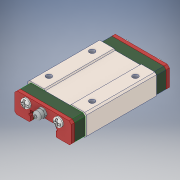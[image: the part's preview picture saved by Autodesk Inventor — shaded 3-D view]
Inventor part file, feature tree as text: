
AUTODESK INVENTOR PART (.ipt)
format: ipt  version: 2018 (Build 220112000, 112)  size: 868,352 bytes
history: native  units: in
note: dims shown in document units (in); Inventor stores cm internally (conversion verified against a paired STEP export)
features: chamfer x3, mirror x3, fillet x2, other x2
ambient origin geometry x8: Origin, YZ Plane, XZ Plane, XY Plane, X Axis, Y Axis, Z Axis, Center Point
bodies: Solid1 (feature_tree), Solid2 (feature_tree), Solid3 (feature_tree), Solid4 (feature_tree), Solid5 (feature_tree), Solid6 (feature_tree), Solid7 (feature_tree), Solid8 (feature_tree), Solid9 (feature_tree), Solid10 (feature_tree)
feature tree (10):
  chamfer  "Chamfer8"  [1 undecoded]
  chamfer  "Chamfer9"  [1 undecoded]
  chamfer  "Chamfer10"  [1 undecoded]
  fillet  "Fillet3"  [1 undecoded]
  mirror  "Mirror9"
  mirror  "Mirror10[1]"
  mirror  "Mirror10[2]"
  fillet  "Fillet5"  [1 undecoded]
  other  "Cut-Extrude9[1]"
  other  "Cut-Extrude9[2]"
note: 5 required parameter values undecoded (feature->parameter linkage not recoverable at this tier; creation-order binding heuristic only, values carry confidence <= 0.55)
